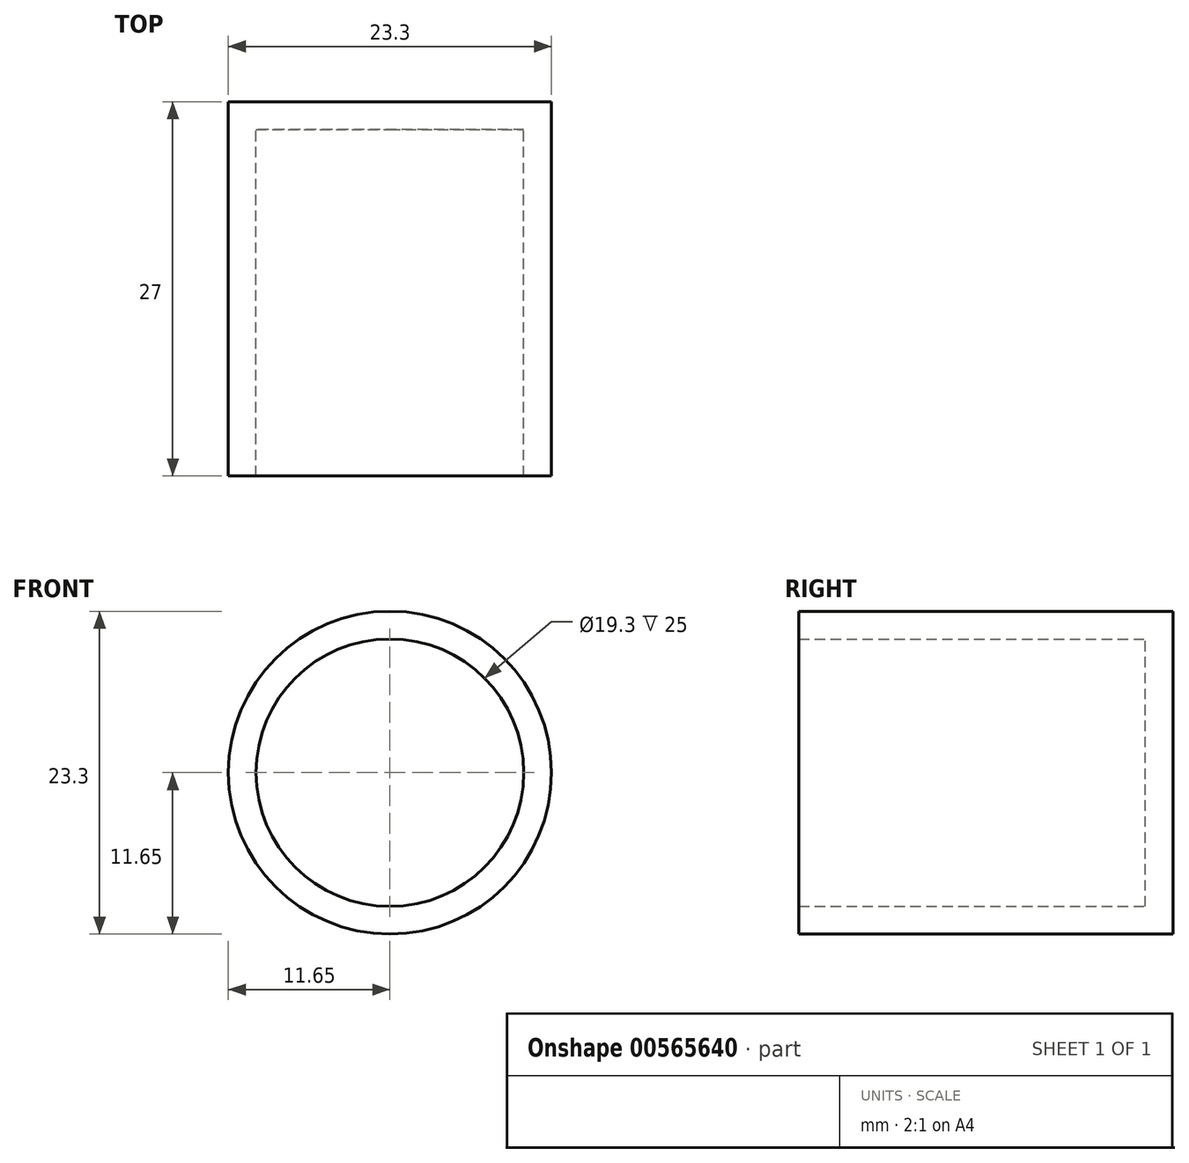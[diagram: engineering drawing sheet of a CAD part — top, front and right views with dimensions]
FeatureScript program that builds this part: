
annotation { "Feature Type Name" : "Feature", "Feature Type Description" : "" }
export const myFeature = defineFeature(function(context is Context, id is Id, definition is map)
    precondition{}
    {
        {
            assignVariable(context, id + "F0", {"variableType" : VariableType.LENGTH, "name" : "height", "lengthValue" : 25 * mm});
        }
        {
            var Q0;
            Q0=qCreatedBy(makeId("Front.planeOp"),FACE);
            var sketch = newSketch(context, id + "F1", { "sketchPlane" : qUnion([Q0])});
            skCircle(sketch, "E0", {"center": v(0, 0) * mm, "radius": 11.65 * mm});
            skCircle(sketch, "E1", {"center": v(0, 0) * mm, "radius": 9.65 * mm});
            skSolve(sketch);
        }
        {
            var Q0;
            Q0=makeQuery(id+"F1.imprint","IMPRINT",FACE,{"disambiguationData":[TD([[makeQuery(id+"F1.imprint","IMPRINT",EDGE,{"derivedFrom":sQuery(id+"F1.wireOp",EDGE,"E0")}),1.0]])]});
            extrude(context, id + "F2", {"entities" : qUnion([Q0]), "depth" : getVariable(context, 'height') + 2 * mm, "offsetDistance" : 25 * mm});
        }
        {
            var Q0;
            Q0=makeQuery(id+"F1.imprint","IMPRINT",FACE,{"disambiguationData":[TD([[makeQuery(id+"F1.imprint","IMPRINT",EDGE,{"derivedFrom":sQuery(id+"F1.wireOp",EDGE,"E1")}),1.0]])]});
            extrude(context, id + "F3", {"entities" : qUnion([Q0]), "operationType" : NewBodyOperationType.ADD, "depth" : 2 * mm, "offsetDistance" : 25 * mm});
        }
    });
